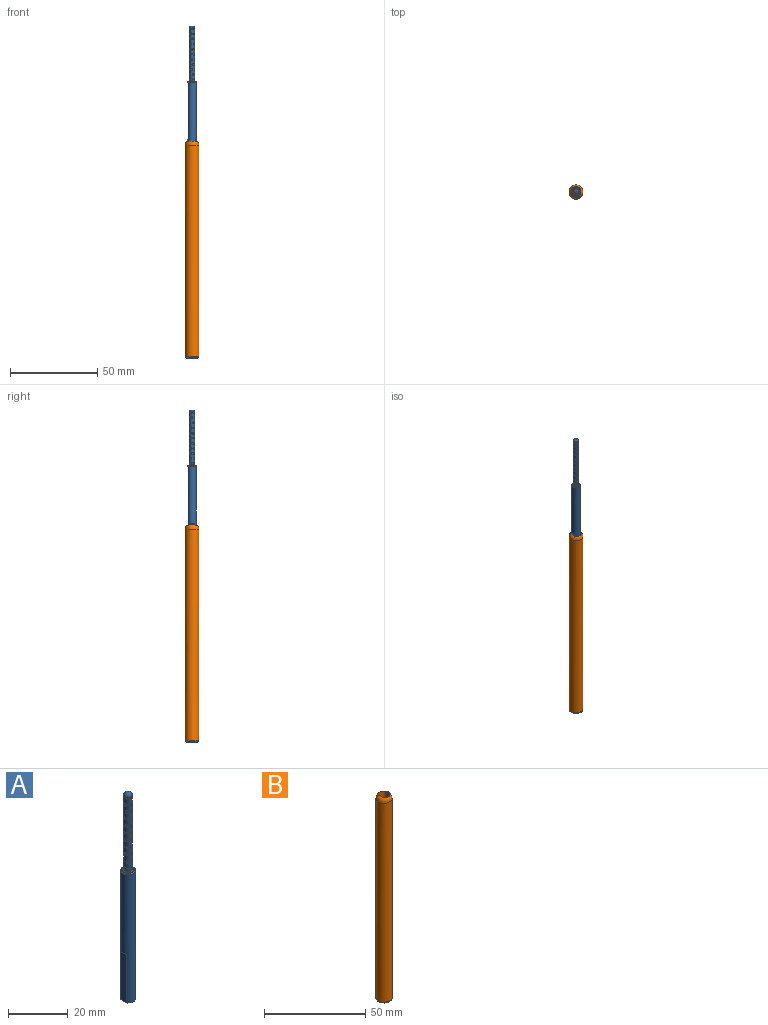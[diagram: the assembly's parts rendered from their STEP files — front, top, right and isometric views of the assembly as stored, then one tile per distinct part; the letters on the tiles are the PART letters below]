
ASSEMBLY  parts=2 mates=1
PART A: 136 faces, bbox 5.4x5.4x85 mm
  f0: cylinder r=2.5mm len=52.65mm, axis (0,0,1), area 698.3mm2, adj f1,f2,f3,f4,f5,f119
  f1: plane 5x4mm, normal (0,0,-1), area 17.6mm2, adj f0,f2,f4
  f2: plane 20x3mm, normal (1,0,0), area 60mm2, adj f0,f1,f3
  f3: plane 3x0.5mm, normal (0,0,-1), area 1mm2, adj f0,f2
  f4: plane 20x3mm, normal (-1,0,0), area 60mm2, adj f0,f1,f5
  f5: plane 3x0.5mm, normal (0,0,-1), area 1mm2, adj f0,f4
  f6: cylinder r=1.5mm len=30.15mm, axis (0,0,1), area 222.9mm2, adj f8,f10,f12,f14,f16,f18,f20,f22
  f7: plane 4.3x4.3mm, normal (0,0,1), area 3.8mm2, adj f118,f119
  f8: cylinder r=0.6mm len=1.2mm, axis (1,0,0), area 0.8mm2, adj f6,f9,f120
  f9: plane 1.2x1.2mm, normal (1,0,0), area 1.1mm2, adj f8
  f10: cylinder r=0.6mm len=1.2mm, axis (0.84,0.54,0.01), area 0.8mm2, adj f6,f11
  f11: plane 1.2x1.01mm, normal (0.84,0.54,0.01), area 1.1mm2, adj f10
  f12: cylinder r=0.6mm len=1.21mm, axis (0.42,0.91,0), area 0.9mm2, adj f6,f13
  f13: plane 1.2x1.09mm, normal (0.42,0.91,0), area 1.1mm2, adj f12
  f14: cylinder r=0.6mm len=1.23mm, axis (-0.14,0.99,0.01), area 0.8mm2, adj f6,f15
  f15: plane 1.2x1.19mm, normal (-0.14,0.99,0.01), area 1.1mm2, adj f14
  f16: cylinder r=0.6mm len=1.2mm, axis (-0.65,0.76,0.01), area 0.9mm2, adj f6,f17
  f17: plane 1.2x0.91mm, normal (-0.65,0.76,0.01), area 1.1mm2, adj f16
  f18: cylinder r=0.6mm len=1.23mm, axis (-0.96,0.28,0.01), area 0.8mm2, adj f6,f19
  f19: plane 1.2x1.15mm, normal (-0.96,0.28,0.01), area 1.1mm2, adj f18
  f20: cylinder r=0.6mm len=1.23mm, axis (-0.96,-0.28,0.01), area 0.8mm2, adj f6,f21
  f21: plane 1.2x1.15mm, normal (-0.96,-0.28,0.01), area 1.1mm2, adj f20
  f22: cylinder r=0.6mm len=1.2mm, axis (-0.66,-0.75,0.01), area 0.9mm2, adj f6,f23
  f23: plane 1.2x0.91mm, normal (-0.66,-0.75,0.01), area 1.1mm2, adj f22
  f24: cylinder r=0.6mm len=1.23mm, axis (-0.15,-0.99,0.01), area 0.8mm2, adj f6,f25
  f25: plane 1.2x1.19mm, normal (-0.15,-0.99,0.01), area 1.1mm2, adj f24
  f26: cylinder r=0.6mm len=1.22mm, axis (0.41,-0.91,0), area 0.9mm2, adj f6,f27
  f27: plane 1.2x1.09mm, normal (0.41,-0.91,0), area 1.1mm2, adj f26
  f28: cylinder r=0.6mm len=1.2mm, axis (0.84,-0.54,0.01), area 0.8mm2, adj f6,f29
  f29: plane 1.2x1.01mm, normal (0.84,-0.54,0.01), area 1.1mm2, adj f28
  f30: cylinder r=0.6mm len=1.23mm, axis (0.31,0.95,0), area 0.8mm2, adj f6,f31,f120
  f31: plane 1.2x1.14mm, normal (0.31,0.95,0), area 1.1mm2, adj f30
  f32: cylinder r=0.6mm len=1.23mm, axis (-0.25,0.97,0.04), area 0.7mm2, adj f6,f33
  f33: plane 1.2x1.16mm, normal (-0.25,0.97,0.04), area 1.1mm2, adj f32
  f34: cylinder r=0.6mm len=1.2mm, axis (-0.74,0.68,0.01), area 0.8mm2, adj f6,f35
  f35: plane 1.2x0.88mm, normal (-0.74,0.68,0.01), area 1.1mm2, adj f34
  f36: cylinder r=0.6mm len=1.23mm, axis (-0.98,0.17,0.03), area 0.7mm2, adj f6,f37
  f37: plane 1.2x1.18mm, normal (-0.98,0.17,0.03), area 1.1mm2, adj f36
  f38: cylinder r=0.6mm len=1.22mm, axis (-0.92,-0.39,0.02), area 0.8mm2, adj f6,f39
  f39: plane 1.2x1.11mm, normal (-0.92,-0.39,0.02), area 1.1mm2, adj f38
  f40: cylinder r=0.6mm len=1.21mm, axis (-0.57,-0.82,0.03), area 0.7mm2, adj f6,f41
  f41: plane 1.2x0.99mm, normal (-0.57,-0.82,0.03), area 1.1mm2, adj f40
  f42: cylinder r=0.6mm len=1.21mm, axis (-0.03,-1,0.03), area 1.2mm2, adj f6,f43
  f43: plane 1.2x1.2mm, normal (-0.03,-1,0.03), area 2.3mm2, adj f42
  f44: cylinder r=0.6mm len=1.21mm, axis (0.51,-0.86,0.02), area 0.8mm2, adj f6,f45
  f45: plane 1.2x1.03mm, normal (0.51,-0.86,0.02), area 1.1mm2, adj f44
  f46: cylinder r=0.6mm len=1.21mm, axis (0.9,-0.44,0.03), area 1.2mm2, adj f6,f47
  f47: plane 1.2x1.08mm, normal (0.9,-0.44,0.03), area 2.3mm2, adj f46
  f48: cylinder r=0.6mm len=1.23mm, axis (0.99,0.11,0.01), area 0.8mm2, adj f6,f49
  f49: plane 1.2x1.19mm, normal (0.99,0.11,0.01), area 1.1mm2, adj f48
  f50: cylinder r=0.6mm len=1.21mm, axis (0.78,0.63,0.04), area 0.7mm2, adj f6,f51
  f51: plane 1.2x0.93mm, normal (0.78,0.63,0.04), area 1.1mm2, adj f50
  f52: cylinder r=0.6mm len=1.2mm, axis (-0.81,0.59,0), area 0.8mm2, adj f6,f53,f120
  f53: plane 1.2x0.97mm, normal (-0.81,0.59,0), area 1.1mm2, adj f52
  f54: cylinder r=0.6mm len=1.22mm, axis (-1,0.06,0.01), area 0.8mm2, adj f6,f55
  f55: plane 1.2x1.2mm, normal (-1,0.06,0.01), area 1.1mm2, adj f54
  f56: cylinder r=0.6mm len=1.2mm, axis (-0.87,-0.49,0), area 0.9mm2, adj f6,f57
  f57: plane 1.2x1.05mm, normal (-0.87,-0.49,0), area 1.1mm2, adj f56
  f58: cylinder r=0.6mm len=1.2mm, axis (-0.47,-0.88,0.01), area 0.8mm2, adj f6,f59
  f59: plane 1.2x1.06mm, normal (-0.47,-0.88,0.01), area 1.1mm2, adj f58
  f60: cylinder r=0.6mm len=1.22mm, axis (0.08,-1,0.01), area 0.9mm2, adj f6,f61
  f61: plane 1.2x1.2mm, normal (0.08,-1,0.01), area 1.1mm2, adj f60
  f62: cylinder r=0.6mm len=1.2mm, axis (0.61,-0.79,0.01), area 0.8mm2, adj f6,f63
  f63: plane 1.2x0.95mm, normal (0.61,-0.79,0.01), area 1.1mm2, adj f62
  f64: cylinder r=0.6mm len=1.23mm, axis (0.94,-0.34,0.01), area 0.8mm2, adj f6,f65
  f65: plane 1.2x1.13mm, normal (0.94,-0.34,0.01), area 1.1mm2, adj f64
  f66: cylinder r=0.6mm len=1.24mm, axis (0.97,0.22,0.01), area 0.9mm2, adj f6,f67
  f67: plane 1.2x1.17mm, normal (0.97,0.22,0.01), area 1.1mm2, adj f66
  f68: cylinder r=0.6mm len=1.2mm, axis (0.7,0.72,0.01), area 0.8mm2, adj f6,f69
  f69: plane 1.2x0.86mm, normal (0.7,0.72,0.01), area 1.1mm2, adj f68
  f70: cylinder r=0.6mm len=1.24mm, axis (0.2,0.98,0), area 0.9mm2, adj f6,f71
  f71: plane 1.2x1.18mm, normal (0.2,0.98,0), area 1.1mm2, adj f70
  f72: cylinder r=0.6mm len=1.22mm, axis (-0.36,0.93,0.01), area 0.8mm2, adj f6,f73
  f73: plane 1.2x1.12mm, normal (-0.36,0.93,0.01), area 1.1mm2, adj f72
  f74: cylinder r=0.6mm len=1.2mm, axis (-0.81,-0.59,0), area 0.8mm2, adj f6,f75,f120
  f75: plane 1.2x0.97mm, normal (-0.81,-0.59,0), area 1.1mm2, adj f74
  f76: cylinder r=0.6mm len=1.22mm, axis (-0.36,-0.93,0.01), area 0.8mm2, adj f6,f77
  f77: plane 1.2x1.12mm, normal (-0.36,-0.93,0.01), area 1.1mm2, adj f76
  f78: cylinder r=0.6mm len=1.24mm, axis (0.2,-0.98,0), area 0.9mm2, adj f6,f79
  f79: plane 1.2x1.18mm, normal (0.2,-0.98,0), area 1.1mm2, adj f78
  f80: cylinder r=0.6mm len=1.2mm, axis (0.7,-0.72,0.01), area 0.8mm2, adj f6,f81
  f81: plane 1.2x0.86mm, normal (0.7,-0.72,0.01), area 1.1mm2, adj f80
  f82: cylinder r=0.6mm len=1.24mm, axis (0.97,-0.23,0.01), area 0.8mm2, adj f6,f83
  f83: plane 1.2x1.17mm, normal (0.97,-0.23,0.01), area 1.1mm2, adj f82
  f84: cylinder r=0.6mm len=1.23mm, axis (0.94,0.34,0.01), area 0.8mm2, adj f6,f85
  f85: plane 1.2x1.13mm, normal (0.94,0.34,0.01), area 1.1mm2, adj f84
  f86: cylinder r=0.6mm len=1.2mm, axis (0.61,0.79,0.01), area 0.8mm2, adj f6,f87
  f87: plane 1.2x0.95mm, normal (0.61,0.79,0.01), area 1.1mm2, adj f86
  f88: cylinder r=0.6mm len=1.22mm, axis (0.08,1,0.01), area 0.8mm2, adj f6,f89
  f89: plane 1.2x1.2mm, normal (0.08,1,0.01), area 1.1mm2, adj f88
  f90: cylinder r=0.6mm len=1.2mm, axis (-0.47,0.88,0.01), area 0.8mm2, adj f6,f91
  f91: plane 1.2x1.06mm, normal (-0.47,0.88,0.01), area 1.1mm2, adj f90
  f92: cylinder r=0.6mm len=1.2mm, axis (-0.87,0.49,0), area 0.9mm2, adj f6,f93
  f93: plane 1.2x1.05mm, normal (-0.87,0.49,0), area 1.1mm2, adj f92
  f94: cylinder r=0.6mm len=1.22mm, axis (-1,-0.06,0.01), area 0.8mm2, adj f6,f95
  f95: plane 1.2x1.2mm, normal (-1,-0.06,0.01), area 1.1mm2, adj f94
  f96: cylinder r=0.6mm len=1.23mm, axis (0.31,-0.95,0), area 0.8mm2, adj f6,f97,f120
  f97: plane 1.2x1.14mm, normal (0.31,-0.95,0), area 1.1mm2, adj f96
  f98: cylinder r=0.6mm len=1.21mm, axis (0.78,-0.63,0.04), area 0.7mm2, adj f6,f99
  f99: plane 1.2x0.93mm, normal (0.78,-0.63,0.04), area 1.1mm2, adj f98
  f100: cylinder r=0.6mm len=1.23mm, axis (0.99,-0.11,0.01), area 0.8mm2, adj f6,f101
  f101: plane 1.2x1.19mm, normal (0.99,-0.11,0.01), area 1.1mm2, adj f100
  f102: cylinder r=0.6mm len=1.21mm, axis (0.9,0.44,0.03), area 0.7mm2, adj f6,f103
  f103: plane 1.2x1.08mm, normal (0.9,0.44,0.03), area 1.1mm2, adj f102
  f104: cylinder r=0.6mm len=1.21mm, axis (0.51,0.86,0.02), area 0.8mm2, adj f6,f105
  f105: plane 1.2x1.03mm, normal (0.51,0.86,0.02), area 1.1mm2, adj f104
  f106: cylinder r=0.6mm len=1.21mm, axis (-0.03,1,0.03), area 0.7mm2, adj f6,f107
  f107: plane 1.2x1.2mm, normal (-0.03,1,0.03), area 1.1mm2, adj f106
  f108: cylinder r=0.6mm len=1.21mm, axis (-0.57,0.82,0.03), area 0.7mm2, adj f6,f109
  f109: plane 1.2x0.99mm, normal (-0.57,0.82,0.03), area 1.1mm2, adj f108
  f110: cylinder r=0.6mm len=1.21mm, axis (-0.92,0.39,0.02), area 0.8mm2, adj f6,f111
  f111: plane 1.2x1.11mm, normal (-0.92,0.39,0.02), area 1.1mm2, adj f110
  f112: cylinder r=0.6mm len=1.23mm, axis (-0.98,-0.17,0.03), area 0.7mm2, adj f6,f113
  f113: plane 1.2x1.18mm, normal (-0.98,-0.17,0.03), area 1.1mm2, adj f112
  f114: cylinder r=0.6mm len=1.2mm, axis (-0.74,-0.68,0.01), area 0.8mm2, adj f6,f115
  f115: plane 1.2x0.88mm, normal (-0.74,-0.68,0.01), area 1.1mm2, adj f114
  f116: cylinder r=0.6mm len=1.23mm, axis (-0.25,-0.97,0.04), area 0.7mm2, adj f6,f117
  f117: plane 1.2x1.16mm, normal (-0.25,-0.97,0.04), area 1.1mm2, adj f116
  f118: torus R=1.85mm, axis (0,0,1), area 5.6mm2, adj f6,f7
  f119: torus R=2.15mm, axis (0,0,1), area 8.2mm2, adj f0,f7
  f120: sphere r=1.5mm, area 11.8mm2, adj f6,f8,f30,f52,f74,f96
  f121: cylinder r=0.6mm len=1.2mm, axis (1,0,0), area 1.1mm2, adj f122,f123
  f122: plane 1.2x1.2mm, normal (1,0,0), area 1.1mm2, adj f121
  f123: plane 1.2x1.2mm, normal (-1,0,0), area 1.1mm2, adj f121
  f124: cylinder r=0.6mm len=1.23mm, axis (0.31,0.95,0), area 1.1mm2, adj f125,f126
  f125: plane 1.2x1.14mm, normal (0.31,0.95,0), area 1.1mm2, adj f124
  f126: plane 1.2x1.14mm, normal (-0.31,-0.95,0), area 1.1mm2, adj f124
  f127: cylinder r=0.6mm len=1.2mm, axis (-0.81,0.59,0), area 1.1mm2, adj f128,f129
  f128: plane 1.2x0.97mm, normal (-0.81,0.59,0), area 1.1mm2, adj f127
  f129: plane 1.2x0.97mm, normal (0.81,-0.59,0), area 1.1mm2, adj f127
  f130: cylinder r=0.6mm len=1.2mm, axis (-0.81,-0.59,0), area 1.1mm2, adj f131,f132
  f131: plane 1.2x0.97mm, normal (-0.81,-0.59,0), area 1.1mm2, adj f130
  f132: plane 1.2x0.97mm, normal (0.81,0.59,0), area 1.1mm2, adj f130
  f133: cylinder r=0.6mm len=1.23mm, axis (0.31,-0.95,0), area 1.1mm2, adj f134,f135
  f134: plane 1.2x1.14mm, normal (0.31,-0.95,0), area 1.1mm2, adj f133
  f135: plane 1.2x1.14mm, normal (-0.31,0.95,0), area 1.1mm2, adj f133
PART B: 9 faces, bbox 8.8x8.8x124.5 mm
  f0: cylinder r=4mm len=120.5mm, axis (0,0,1), area 3028.5mm2, adj f7,f8
  f1: plane 6x6mm, normal (0,0,-1), area 28.3mm2, adj f8
  f2: plane 19.53x3.47mm, normal (-1,0,0), area 63.8mm2, adj f3,f5,f6,f7
  f3: cylinder r=3mm len=18.95mm, axis (0,0,1), area 112mm2, adj f2,f4,f6,f7
  f4: plane 19.37x3.32mm, normal (1,0,0), area 63.8mm2, adj f3,f5,f6,f7
  f5: cylinder r=3mm len=18.95mm, axis (0,0,1), area 112mm2, adj f2,f4,f6,f7
  f6: plane 6x5mm, normal (0,0,1), area 26mm2, adj f2,f3,f4,f5
  f7: torus R=0.5mm, axis (0,0,-1), area 65.3mm2, adj f0,f2,f3,f4,f5
  f8: torus R=3mm, axis (0,0,1), area 35.9mm2, adj f0,f1
PLACE A t=(0,0,85)mm
PLACE B at identity
MATE fastened A.f0 <-> B.f0  axis (0,0,-1) through (0,0,42.5)mm
